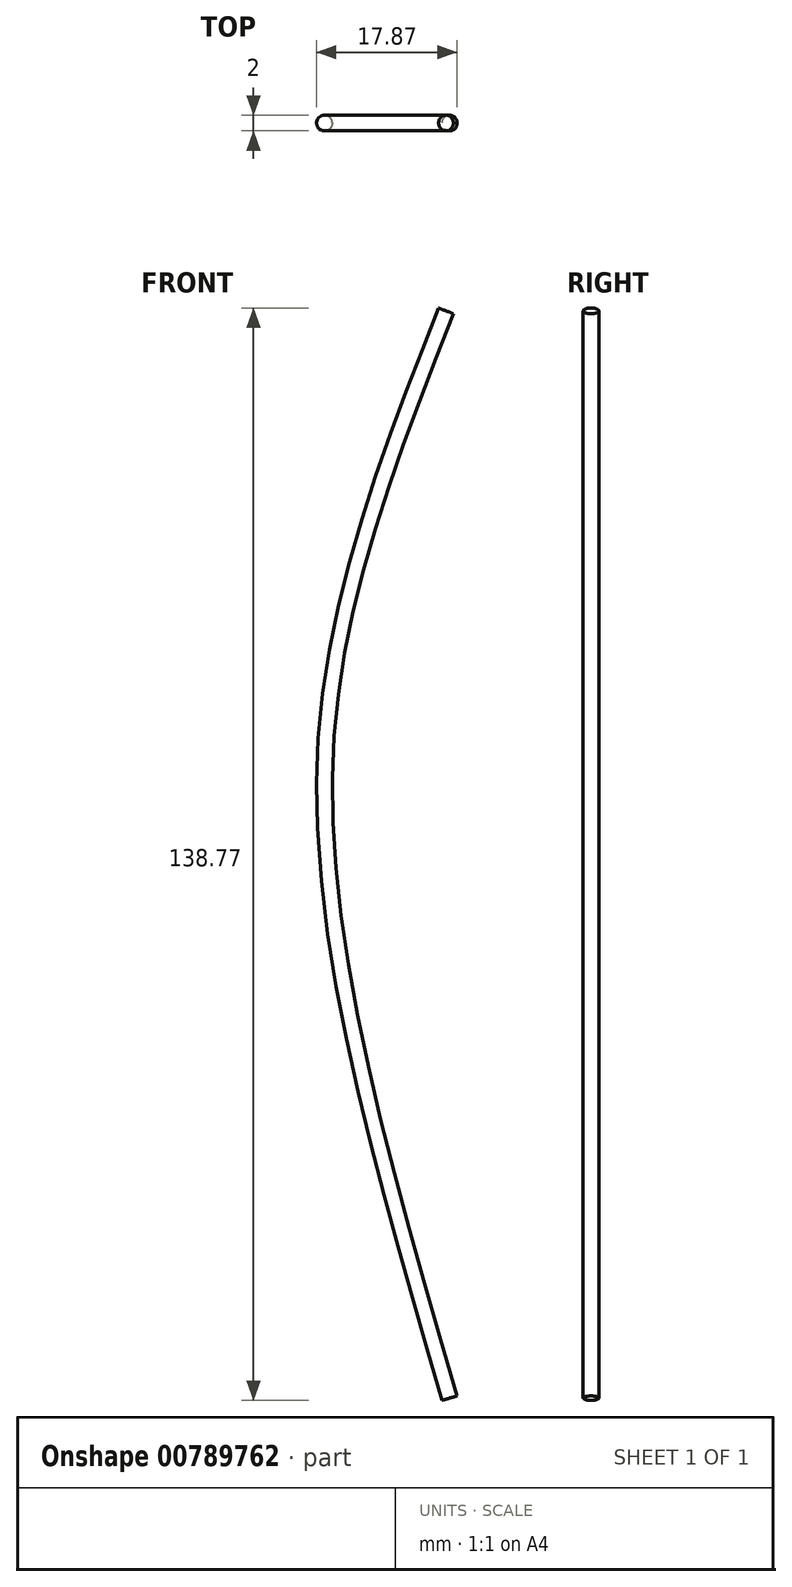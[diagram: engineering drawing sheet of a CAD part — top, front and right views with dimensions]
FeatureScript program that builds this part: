
annotation { "Feature Type Name" : "Feature", "Feature Type Description" : "" }
export const myFeature = defineFeature(function(context is Context, id is Id, definition is map)
    precondition{}
    {
        {
            var Q0;
            Q0=qCreatedBy(makeId("Front.planeOp"),FACE);
            var sketch = newSketch(context, id + "F0", { "sketchPlane" : qUnion([Q0])});
            skFitSpline(sketch, "E0", {"points": [v(0, -73.82) * mm, v(-16.49, 11.87) * mm, v(0, 74.66) * mm], "startDerivative": vector(-48.5, 166.03) * mm, "endDerivative": vector(50.95, 130.03) * mm});
            skSolve(sketch);
        }
        {
            var Q0;
            Q0=sQuery(id+"F0.wireOp",VERTEX,"E0.end");
            var Q1;
            Q1=sQuery(id+"F0.wireOp",EDGE,"E0");
            cPlane(context, id + "F1", {"entities" : qUnion([Q0, Q1]), "cplaneType" : CPlaneType.CURVE_POINT, "offset" : 25 * mm, "width" : 150 * mm, "height" : 150 * mm});
        }
        {
            var Q0;
            Q0=qCreatedBy(id+"F1.planeOp",FACE);
            var sketch = newSketch(context, id + "F2", { "sketchPlane" : qUnion([Q0])});
            skCircle(sketch, "E1", {"center": v(-11.2, 0) * mm, "radius": 1 * mm});
            skSolve(sketch);
        }
        {
            var Q0;
            Q0=makeQuery(id+"F2.imprint","IMPRINT",FACE,{"disambiguationData":[TD([[makeQuery(id+"F2.imprint","IMPRINT",EDGE,{"derivedFrom":sQuery(id+"F2.wireOp",EDGE,"E1")}),1.0]])]});
            var Q1;
            Q1=sQuery(id+"F0.wireOp",EDGE,"E0");
            sweep(context, id + "F3", {"profiles" : qUnion([Q0]), "path" : qUnion([Q1])});
        }
    });
